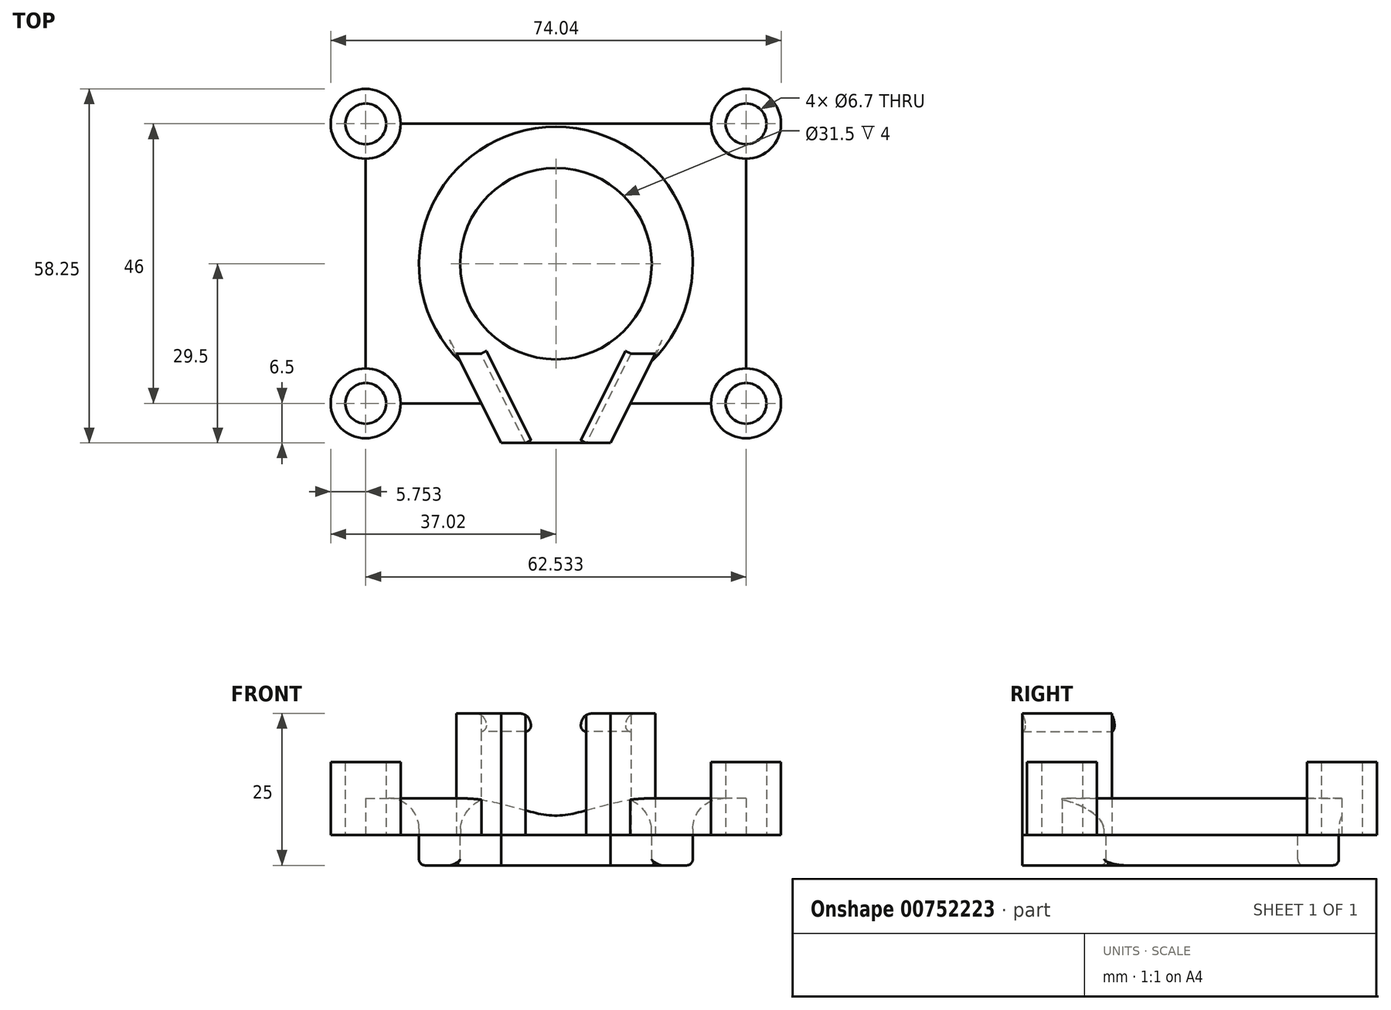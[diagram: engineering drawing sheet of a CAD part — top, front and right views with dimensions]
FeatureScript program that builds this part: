
annotation { "Feature Type Name" : "Feature", "Feature Type Description" : "" }
export const myFeature = defineFeature(function(context is Context, id is Id, definition is map)
    precondition{}
    {
        {
            var Q0;
            Q0=qCreatedBy(makeId("Top.planeOp"),FACE);
            var sketch = newSketch(context, id + "F0", { "sketchPlane" : qUnion([Q0])});
            skCircle(sketch, "E0", {"center": v(-31.27, 23) * mm, "radius": 5.75 * mm});
            skCircle(sketch, "E1", {"center": v(31.27, -23) * mm, "radius": 5.75 * mm});
            skCircle(sketch, "E2", {"center": v(31.27, -23) * mm, "radius": 3.35 * mm});
            skCircle(sketch, "E3", {"center": v(-31.27, 23) * mm, "radius": 3.35 * mm});
            skLineSegment(sketch, "E4", {"start": v(-31.27, 23) * mm, "end": v(31.27, -23) * mm});
            skCircle(sketch, "E5", {"center": v(0, 0) * mm, "radius": 22.5 * mm});
            skCircle(sketch, "E6", {"center": v(0, 0) * mm, "radius": 15.75 * mm});
            skLineSegment(sketch, "E7", {"start": v(-31.27, 23) * mm, "end": v(-31.27, -23) * mm});
            skLineSegment(sketch, "E8", {"start": v(-31.27, -23) * mm, "end": v(31.27, -23) * mm});
            skCircle(sketch, "E9", {"center": v(-31.27, -23) * mm, "radius": 5.75 * mm});
            skCircle(sketch, "E10", {"center": v(-31.27, -23) * mm, "radius": 3.35 * mm});
            skLineSegment(sketch, "E11", {"start": v(-31.27, 23) * mm, "end": v(31.27, 23) * mm});
            skCircle(sketch, "E12", {"center": v(31.27, 23) * mm, "radius": 5.75 * mm});
            skCircle(sketch, "E13", {"center": v(31.27, 23) * mm, "radius": 3.35 * mm});
            skLineSegment(sketch, "E14", {"start": v(31.27, -23) * mm, "end": v(31.27, 23) * mm});
            skLineSegment(sketch, "E15", {"start": v(0, 0) * mm, "end": v(0, -29.5) * mm});
            skLineSegment(sketch, "E16", {"start": v(-5, -29.5) * mm, "end": v(5, -29.5) * mm});
            skLineSegment(sketch, "E17", {"start": v(-5, -29.5) * mm, "end": v(-9, -29.5) * mm});
            skLineSegment(sketch, "E18", {"start": v(5, -29.5) * mm, "end": v(9, -29.5) * mm});
            skLineSegment(sketch, "E19", {"start": v(-5, -29.5) * mm, "end": v(-12.33, -14.82) * mm});
            skLineSegment(sketch, "E20", {"start": v(-12.33, -14.82) * mm, "end": v(12.33, -14.82) * mm});
            skLineSegment(sketch, "E21", {"start": v(12.33, -14.82) * mm, "end": v(5, -29.5) * mm});
            skLineSegment(sketch, "E22", {"start": v(-12.33, -14.82) * mm, "end": v(-16.33, -14.82) * mm});
            skLineSegment(sketch, "E23", {"start": v(-16.33, -14.82) * mm, "end": v(-9, -29.5) * mm});
            skLineSegment(sketch, "E24", {"start": v(9, -29.5) * mm, "end": v(16.32, -14.82) * mm});
            skLineSegment(sketch, "E25", {"start": v(16.32, -14.82) * mm, "end": v(12.33, -14.82) * mm});
            skSolve(sketch);
        }
        {
            var Q0;
            {var subQ0=sQuery(id+"F0.wireOp",EDGE,"E9");var subQ1=sQuery(id+"F0.wireOp",EDGE,"E7");var subQ2=makeQuery(id+"F0.imprint","INTERSECT",VERTEX,{"derivedFrom":[subQ1,subQ0]});Q0=makeQuery(id+"F0.imprint","IMPRINT",FACE,{"disambiguationData":[TD([[makeQuery(id+"F0.imprint","IMPRINT",EDGE,{"disambiguationData":[TD([[subQ2,-1.0]])],"derivedFrom":subQ1}),-1.0]])]});}
            var Q1;
            {var subQ0=sQuery(id+"F0.wireOp",EDGE,"E12");var subQ1=sQuery(id+"F0.wireOp",EDGE,"E11");var subQ2=makeQuery(id+"F0.imprint","INTERSECT",VERTEX,{"derivedFrom":[subQ1,subQ0]});Q1=makeQuery(id+"F0.imprint","IMPRINT",FACE,{"disambiguationData":[TD([[makeQuery(id+"F0.imprint","IMPRINT",EDGE,{"disambiguationData":[TD([[subQ2,-1.0]])],"derivedFrom":subQ1}),1.0]])]});}
            var Q2;
            {var subQ0=sQuery(id+"F0.wireOp",EDGE,"E7");var subQ1=sQuery(id+"F0.wireOp",EDGE,"E0");var subQ2=makeQuery(id+"F0.imprint","INTERSECT",VERTEX,{"derivedFrom":[subQ1,subQ0]});Q2=makeQuery(id+"F0.imprint","IMPRINT",FACE,{"disambiguationData":[TD([[makeQuery(id+"F0.imprint","IMPRINT",EDGE,{"disambiguationData":[TD([[subQ2,1.0]])],"derivedFrom":subQ1}),1.0]])]});}
            var Q3;
            {var subQ0=sQuery(id+"F0.wireOp",EDGE,"E14");var subQ1=sQuery(id+"F0.wireOp",EDGE,"E1");var subQ2=makeQuery(id+"F0.imprint","INTERSECT",VERTEX,{"derivedFrom":[subQ1,subQ0]});Q3=makeQuery(id+"F0.imprint","IMPRINT",FACE,{"disambiguationData":[TD([[makeQuery(id+"F0.imprint","IMPRINT",EDGE,{"disambiguationData":[TD([[subQ2,1.0]])],"derivedFrom":subQ1}),1.0]])]});}
            var Q4;
            {var subQ0=sQuery(id+"F0.wireOp",EDGE,"E9");var subQ1=sQuery(id+"F0.wireOp",EDGE,"E7");var subQ2=makeQuery(id+"F0.imprint","INTERSECT",VERTEX,{"derivedFrom":[subQ1,subQ0]});Q4=makeQuery(id+"F0.imprint","IMPRINT",FACE,{"disambiguationData":[TD([[makeQuery(id+"F0.imprint","IMPRINT",EDGE,{"disambiguationData":[TD([[subQ2,-1.0]])],"derivedFrom":subQ1}),1.0]])]});}
            var Q5;
            {var subQ0=sQuery(id+"F0.wireOp",EDGE,"E12");var subQ1=sQuery(id+"F0.wireOp",EDGE,"E11");var subQ2=makeQuery(id+"F0.imprint","INTERSECT",VERTEX,{"derivedFrom":[subQ1,subQ0]});Q5=makeQuery(id+"F0.imprint","IMPRINT",FACE,{"disambiguationData":[TD([[makeQuery(id+"F0.imprint","IMPRINT",EDGE,{"disambiguationData":[TD([[subQ2,-1.0]])],"derivedFrom":subQ1}),-1.0]])]});}
            var Q6;
            {var subQ0=sQuery(id+"F0.wireOp",EDGE,"E7");var subQ1=sQuery(id+"F0.wireOp",EDGE,"E0");var subQ2=makeQuery(id+"F0.imprint","INTERSECT",VERTEX,{"derivedFrom":[subQ1,subQ0]});Q6=makeQuery(id+"F0.imprint","IMPRINT",FACE,{"disambiguationData":[TD([[makeQuery(id+"F0.imprint","IMPRINT",EDGE,{"disambiguationData":[TD([[subQ2,-1.0]])],"derivedFrom":subQ1}),1.0]])]});}
            var Q7;
            {var subQ0=sQuery(id+"F0.wireOp",EDGE,"E11");var subQ1=sQuery(id+"F0.wireOp",EDGE,"E0");var subQ2=makeQuery(id+"F0.imprint","INTERSECT",VERTEX,{"derivedFrom":[subQ1,subQ0]});Q7=makeQuery(id+"F0.imprint","IMPRINT",FACE,{"disambiguationData":[TD([[makeQuery(id+"F0.imprint","IMPRINT",EDGE,{"disambiguationData":[TD([[subQ2,1.0]])],"derivedFrom":subQ1}),1.0]])]});}
            var Q8;
            {var subQ0=sQuery(id+"F0.wireOp",EDGE,"E14");var subQ1=sQuery(id+"F0.wireOp",EDGE,"E1");var subQ2=makeQuery(id+"F0.imprint","INTERSECT",VERTEX,{"derivedFrom":[subQ1,subQ0]});Q8=makeQuery(id+"F0.imprint","IMPRINT",FACE,{"disambiguationData":[TD([[makeQuery(id+"F0.imprint","IMPRINT",EDGE,{"disambiguationData":[TD([[subQ2,-1.0]])],"derivedFrom":subQ1}),1.0]])]});}
            var Q9;
            {var subQ0=sQuery(id+"F0.wireOp",EDGE,"E8");var subQ1=sQuery(id+"F0.wireOp",EDGE,"E1");var subQ2=makeQuery(id+"F0.imprint","INTERSECT",VERTEX,{"derivedFrom":[subQ1,subQ0]});Q9=makeQuery(id+"F0.imprint","IMPRINT",FACE,{"disambiguationData":[TD([[makeQuery(id+"F0.imprint","IMPRINT",EDGE,{"disambiguationData":[TD([[subQ2,1.0]])],"derivedFrom":subQ1}),1.0]])]});}
            extrude(context, id + "F1", {"entities" : qUnion([Q0, Q1, Q2, Q3, Q4, Q5, Q6, Q7, Q8, Q9]), "depth" : 12 * mm, "offsetDistance" : 25 * mm});
        }
        {
            var Q0;
            {var subQ0=sQuery(id+"F0.wireOp",EDGE,"E5");var subQ1=sQuery(id+"F0.wireOp",EDGE,"E4");var subQ2=makeQuery(id+"F0.imprint","INTERSECT",VERTEX,{"disambiguationData":[OD(0.0)],"derivedFrom":[subQ1,subQ0]});Q0=makeQuery(id+"F0.imprint","IMPRINT",FACE,{"disambiguationData":[TD([[makeQuery(id+"F0.imprint","IMPRINT",EDGE,{"disambiguationData":[TD([[subQ2,-1.0]])],"derivedFrom":subQ1}),1.0]])]});}
            var Q1;
            {var subQ0=sQuery(id+"F0.wireOp",EDGE,"E5");var subQ1=sQuery(id+"F0.wireOp",EDGE,"E4");var subQ2=makeQuery(id+"F0.imprint","INTERSECT",VERTEX,{"disambiguationData":[OD(0.0)],"derivedFrom":[subQ1,subQ0]});Q1=makeQuery(id+"F0.imprint","IMPRINT",FACE,{"disambiguationData":[TD([[makeQuery(id+"F0.imprint","IMPRINT",EDGE,{"disambiguationData":[TD([[subQ2,-1.0]])],"derivedFrom":subQ1}),-1.0]])]});}
            var Q2;
            {var subQ0=sQuery(id+"F0.wireOp",EDGE,"E25");Q2=makeQuery(id+"F0.imprint","IMPRINT",FACE,{"disambiguationData":[TD([[makeQuery(id+"F0.imprint","IMPRINT",EDGE,{"derivedFrom":subQ0}),-1.0]])]});}
            var Q3;
            {var subQ5=sQuery(id+"F0.wireOp",EDGE,"E25");Q3=makeQuery(id+"F0.imprint","IMPRINT",FACE,{"disambiguationData":[TD([[makeQuery(id+"F0.imprint","IMPRINT",EDGE,{"derivedFrom":subQ5}),1.0]])]});}
            var Q4;
            {var subQ5=sQuery(id+"F0.wireOp",EDGE,"E15");var subQ6=sQuery(id+"F0.wireOp",EDGE,"E5");var subQ7=makeQuery(id+"F0.imprint","INTERSECT",VERTEX,{"derivedFrom":[subQ6,subQ5]});Q4=makeQuery(id+"F0.imprint","IMPRINT",FACE,{"disambiguationData":[TD([[makeQuery(id+"F0.imprint","IMPRINT",EDGE,{"disambiguationData":[TD([[subQ7,-1.0]])],"derivedFrom":subQ6}),1.0]])]});}
            var Q5;
            {var subQ1=sQuery(id+"F0.wireOp",EDGE,"E19");var subQ3=sQuery(id+"F0.wireOp",EDGE,"E5");var subQ4=makeQuery(id+"F0.imprint","INTERSECT",VERTEX,{"derivedFrom":[subQ3,subQ1]});Q5=makeQuery(id+"F0.imprint","IMPRINT",FACE,{"disambiguationData":[TD([[makeQuery(id+"F0.imprint","IMPRINT",EDGE,{"disambiguationData":[TD([[subQ4,-1.0]])],"derivedFrom":subQ3}),1.0]])]});}
            var Q6;
            {var subQ5=sQuery(id+"F0.wireOp",EDGE,"E22");Q6=makeQuery(id+"F0.imprint","IMPRINT",FACE,{"disambiguationData":[TD([[makeQuery(id+"F0.imprint","IMPRINT",EDGE,{"derivedFrom":subQ5}),1.0]])]});}
            var Q7;
            {var subQ0=sQuery(id+"F0.wireOp",EDGE,"E23");var subQ1=sQuery(id+"F0.wireOp",EDGE,"E5");var subQ2=makeQuery(id+"F0.imprint","INTERSECT",VERTEX,{"derivedFrom":[subQ1,subQ0]});Q7=makeQuery(id+"F0.imprint","IMPRINT",FACE,{"disambiguationData":[TD([[makeQuery(id+"F0.imprint","IMPRINT",EDGE,{"disambiguationData":[TD([[subQ2,-1.0]])],"derivedFrom":subQ1}),-1.0]])]});}
            var Q8;
            {var subQ5=sQuery(id+"F0.wireOp",EDGE,"E17");Q8=makeQuery(id+"F0.imprint","IMPRINT",FACE,{"disambiguationData":[TD([[makeQuery(id+"F0.imprint","IMPRINT",EDGE,{"derivedFrom":subQ5}),-1.0]])]});}
            var Q9;
            {var subQ0=sQuery(id+"F0.wireOp",EDGE,"E19");var subQ1=sQuery(id+"F0.wireOp",EDGE,"E8");var subQ2=makeQuery(id+"F0.imprint","INTERSECT",VERTEX,{"derivedFrom":[subQ1,subQ0]});Q9=makeQuery(id+"F0.imprint","IMPRINT",FACE,{"disambiguationData":[TD([[makeQuery(id+"F0.imprint","IMPRINT",EDGE,{"disambiguationData":[TD([[subQ2,-1.0]])],"derivedFrom":subQ1}),-1.0]])]});}
            var Q10;
            {var subQ0=sQuery(id+"F0.wireOp",EDGE,"E19");var subQ1=sQuery(id+"F0.wireOp",EDGE,"E5");var subQ2=makeQuery(id+"F0.imprint","INTERSECT",VERTEX,{"derivedFrom":[subQ1,subQ0]});Q10=makeQuery(id+"F0.imprint","IMPRINT",FACE,{"disambiguationData":[TD([[makeQuery(id+"F0.imprint","IMPRINT",EDGE,{"disambiguationData":[TD([[subQ2,-1.0]])],"derivedFrom":subQ1}),-1.0]])]});}
            var Q11;
            {var subQ0=sQuery(id+"F0.wireOp",EDGE,"E15");var subQ1=sQuery(id+"F0.wireOp",EDGE,"E8");var subQ2=makeQuery(id+"F0.imprint","INTERSECT",VERTEX,{"derivedFrom":[subQ1,subQ0]});Q11=makeQuery(id+"F0.imprint","IMPRINT",FACE,{"disambiguationData":[TD([[makeQuery(id+"F0.imprint","IMPRINT",EDGE,{"disambiguationData":[TD([[subQ2,-1.0]])],"derivedFrom":subQ1}),-1.0]])]});}
            var Q12;
            {var subQ0=sQuery(id+"F0.wireOp",EDGE,"E15");var subQ1=sQuery(id+"F0.wireOp",EDGE,"E5");var subQ2=makeQuery(id+"F0.imprint","INTERSECT",VERTEX,{"derivedFrom":[subQ1,subQ0]});Q12=makeQuery(id+"F0.imprint","IMPRINT",FACE,{"disambiguationData":[TD([[makeQuery(id+"F0.imprint","IMPRINT",EDGE,{"disambiguationData":[TD([[subQ2,-1.0]])],"derivedFrom":subQ1}),-1.0]])]});}
            var Q13;
            {var subQ5=sQuery(id+"F0.wireOp",EDGE,"E18");Q13=makeQuery(id+"F0.imprint","IMPRINT",FACE,{"disambiguationData":[TD([[makeQuery(id+"F0.imprint","IMPRINT",EDGE,{"derivedFrom":subQ5}),1.0]])]});}
            var Q14;
            {var subQ0=sQuery(id+"F0.wireOp",EDGE,"E21");var subQ1=sQuery(id+"F0.wireOp",EDGE,"E5");var subQ2=makeQuery(id+"F0.imprint","INTERSECT",VERTEX,{"derivedFrom":[subQ1,subQ0]});Q14=makeQuery(id+"F0.imprint","IMPRINT",FACE,{"disambiguationData":[TD([[makeQuery(id+"F0.imprint","IMPRINT",EDGE,{"disambiguationData":[TD([[subQ2,-1.0]])],"derivedFrom":subQ1}),-1.0]])]});}
            extrude(context, id + "F2", {"entities" : qUnion([Q0, Q1, Q2, Q3, Q4, Q5, Q6, Q7, Q8, Q9, Q10, Q11, Q12, Q13, Q14]), "depth" : -5 * mm, "offsetDistance" : 25 * mm});
        }
        {
            var Q0;
            {var subQ5=sQuery(id+"F0.wireOp",EDGE,"E0");var subQ11=sQuery(id+"F0.wireOp",EDGE,"E11");var subQ14=makeQuery(id+"F0.imprint","INTERSECT",VERTEX,{"derivedFrom":[subQ5,subQ11]});Q0=makeQuery(id+"F0.imprint","IMPRINT",FACE,{"disambiguationData":[TD([[makeQuery(id+"F0.imprint","IMPRINT",EDGE,{"disambiguationData":[TD([[subQ14,1.0]])],"derivedFrom":subQ5}),-1.0]])]});}
            var Q1;
            {var subQ7=sQuery(id+"F0.wireOp",EDGE,"E0");var subQ9=sQuery(id+"F0.wireOp",EDGE,"E7");var subQ10=makeQuery(id+"F0.imprint","INTERSECT",VERTEX,{"derivedFrom":[subQ7,subQ9]});Q1=makeQuery(id+"F0.imprint","IMPRINT",FACE,{"disambiguationData":[TD([[makeQuery(id+"F0.imprint","IMPRINT",EDGE,{"disambiguationData":[TD([[subQ10,-1.0]])],"derivedFrom":subQ7}),-1.0]])]});}
            var Q2;
            {var subQ0=sQuery(id+"F0.wireOp",EDGE,"E8");var subQ1=sQuery(id+"F0.wireOp",EDGE,"E1");var subQ2=makeQuery(id+"F0.imprint","INTERSECT",VERTEX,{"derivedFrom":[subQ1,subQ0]});Q2=makeQuery(id+"F0.imprint","IMPRINT",FACE,{"disambiguationData":[TD([[makeQuery(id+"F0.imprint","IMPRINT",EDGE,{"disambiguationData":[TD([[subQ2,1.0]])],"derivedFrom":subQ1}),-1.0]])]});}
            extrude(context, id + "F3", {"entities" : qUnion([Q0, Q1, Q2]), "depth" : 6 * mm, "offsetDistance" : 25 * mm});
        }
        {
            var Q0;
            Q0=makeQuery(id+"F3.opExtrude","CAP_EDGE",EDGE,{"disambiguationData":[OSD([sQuery(id+"F0.wireOp",EDGE,"E5")])],"isStart":false});
            fillet(context, id + "F4", {"entities" : qUnion([Q0]), "radius" : 5 * mm, "tangentPropagation" : true, "allowEdgeOverflow" : false});
        }
        {
            var Q0;
            {var subQ5=sQuery(id+"F0.wireOp",EDGE,"E22");Q0=makeQuery(id+"F0.imprint","IMPRINT",FACE,{"disambiguationData":[TD([[makeQuery(id+"F0.imprint","IMPRINT",EDGE,{"derivedFrom":subQ5}),1.0]])]});}
            var Q1;
            {var subQ0=sQuery(id+"F0.wireOp",EDGE,"E23");var subQ1=sQuery(id+"F0.wireOp",EDGE,"E5");var subQ2=makeQuery(id+"F0.imprint","INTERSECT",VERTEX,{"derivedFrom":[subQ1,subQ0]});Q1=makeQuery(id+"F0.imprint","IMPRINT",FACE,{"disambiguationData":[TD([[makeQuery(id+"F0.imprint","IMPRINT",EDGE,{"disambiguationData":[TD([[subQ2,-1.0]])],"derivedFrom":subQ1}),-1.0]])]});}
            var Q2;
            {var subQ5=sQuery(id+"F0.wireOp",EDGE,"E17");Q2=makeQuery(id+"F0.imprint","IMPRINT",FACE,{"disambiguationData":[TD([[makeQuery(id+"F0.imprint","IMPRINT",EDGE,{"derivedFrom":subQ5}),-1.0]])]});}
            var Q3;
            {var subQ5=sQuery(id+"F0.wireOp",EDGE,"E18");Q3=makeQuery(id+"F0.imprint","IMPRINT",FACE,{"disambiguationData":[TD([[makeQuery(id+"F0.imprint","IMPRINT",EDGE,{"derivedFrom":subQ5}),1.0]])]});}
            var Q4;
            {var subQ0=sQuery(id+"F0.wireOp",EDGE,"E21");var subQ1=sQuery(id+"F0.wireOp",EDGE,"E5");var subQ2=makeQuery(id+"F0.imprint","INTERSECT",VERTEX,{"derivedFrom":[subQ1,subQ0]});Q4=makeQuery(id+"F0.imprint","IMPRINT",FACE,{"disambiguationData":[TD([[makeQuery(id+"F0.imprint","IMPRINT",EDGE,{"disambiguationData":[TD([[subQ2,-1.0]])],"derivedFrom":subQ1}),-1.0]])]});}
            var Q5;
            {var subQ5=sQuery(id+"F0.wireOp",EDGE,"E25");Q5=makeQuery(id+"F0.imprint","IMPRINT",FACE,{"disambiguationData":[TD([[makeQuery(id+"F0.imprint","IMPRINT",EDGE,{"derivedFrom":subQ5}),1.0]])]});}
            extrude(context, id + "F5", {"entities" : qUnion([Q0, Q1, Q2, Q3, Q4, Q5]), "depth" : 20 * mm, "offsetDistance" : 25 * mm});
        }
        {
            var Q0;
            Q0=makeQuery(id+"F5.opExtrude","SWEPT_FACE",FACE,{"disambiguationData":[OSD([sQuery(id+"F0.wireOp",EDGE,"E19")])]});
            var sketch = newSketch(context, id + "F6", { "sketchPlane" : qUnion([Q0])});
            skLineSegment(sketch, "E26.bottom", {"start": v(-24.16, 20) * mm, "end": v(-7.76, 20) * mm});
            skLineSegment(sketch, "E26.top", {"start": v(-24.16, 17) * mm, "end": v(-7.76, 17) * mm});
            skLineSegment(sketch, "E26.left", {"start": v(-24.16, 20) * mm, "end": v(-24.16, 17) * mm});
            skLineSegment(sketch, "E26.right", {"start": v(-7.76, 20) * mm, "end": v(-7.76, 17) * mm});
            skSolve(sketch);
        }
        {
            var Q0;
            Q0 = qSketchRegion(id + "F6", true);
            extrude(context, id + "F7", {"entities" : qUnion([Q0]), "operationType" : NewBodyOperationType.ADD, "depth" : 1 * mm, "offsetDistance" : 25 * mm});
        }
        {
            var Q0;
            Q0=makeQuery(id+"F7.opExtrude","CAP_EDGE",EDGE,{"disambiguationData":[OSD([sQuery(id+"F6.wireOp",EDGE,"E26.bottom")])],"isStart":false});
            fillet(context, id + "F8", {"entities" : qUnion([Q0]), "radius" : 2 * mm, "tangentPropagation" : true, "allowEdgeOverflow" : false});
        }
        {
            var Q0;
            Q0=makeQuery(id+"F7.opExtrude","CAP_EDGE",EDGE,{"disambiguationData":[OSD([sQuery(id+"F6.wireOp",EDGE,"E26.top")])],"isStart":false});
            fillet(context, id + "F9", {"entities" : qUnion([Q0]), "radius" : 1 * mm, "tangentPropagation" : true, "allowEdgeOverflow" : false});
        }
        {
            var Q0;
            Q0=makeQuery(id+"F5.opExtrude","SWEPT_FACE",FACE,{"disambiguationData":[OSD([sQuery(id+"F0.wireOp",EDGE,"E21")])]});
            var sketch = newSketch(context, id + "F10", { "sketchPlane" : qUnion([Q0])});
            skLineSegment(sketch, "E27.bottom", {"start": v(7.76, 20) * mm, "end": v(24.16, 20) * mm});
            skLineSegment(sketch, "E27.top", {"start": v(7.76, 17) * mm, "end": v(24.16, 17) * mm});
            skLineSegment(sketch, "E27.left", {"start": v(7.76, 20) * mm, "end": v(7.76, 17) * mm});
            skLineSegment(sketch, "E27.right", {"start": v(24.16, 20) * mm, "end": v(24.16, 17) * mm});
            skSolve(sketch);
        }
        {
            var Q0;
            Q0=makeQuery(id+"F10.imprint","IMPRINT",FACE,{"disambiguationData":[TD([[makeQuery(id+"F10.imprint","IMPRINT",EDGE,{"derivedFrom":sQuery(id+"F10.wireOp",EDGE,"E27.bottom")}),-1.0]])]});
            extrude(context, id + "F11", {"entities" : qUnion([Q0]), "operationType" : NewBodyOperationType.ADD, "depth" : 1 * mm, "offsetDistance" : 25 * mm});
        }
        {
            var Q0;
            Q0=makeQuery(id+"F11.opExtrude","CAP_EDGE",EDGE,{"disambiguationData":[OSD([sQuery(id+"F10.wireOp",EDGE,"E27.bottom")])],"isStart":false});
            fillet(context, id + "F12", {"entities" : qUnion([Q0]), "radius" : 2 * mm, "tangentPropagation" : true, "allowEdgeOverflow" : false});
        }
        {
            var Q0;
            Q0=makeQuery(id+"F11.opExtrude","CAP_EDGE",EDGE,{"disambiguationData":[OSD([sQuery(id+"F10.wireOp",EDGE,"E27.top")])],"isStart":false});
            fillet(context, id + "F13", {"entities" : qUnion([Q0]), "radius" : 1 * mm, "tangentPropagation" : true, "allowEdgeOverflow" : false});
        }
        {
            var Q0;
            Q0=makeQuery(id+"F2.opExtrude","CAP_EDGE",EDGE,{"disambiguationData":[OSD([sQuery(id+"F0.wireOp",EDGE,"E5")])],"isStart":false});
            fillet(context, id + "F14", {"entities" : qUnion([Q0]), "radius" : 1 * mm, "tangentPropagation" : true, "allowEdgeOverflow" : false});
        }
        {
            var Q0;
            Q0=makeQuery(id+"F14.opFillet","BLEND_FACE",FACE,{"disambiguationData":[OSD([sQuery(id+"F0.wireOp",EDGE,"E5")])]});
            fillet(context, id + "F15", {"entities" : qUnion([Q0]), "radius" : 1 * mm, "tangentPropagation" : true, "allowEdgeOverflow" : false});
        }
        {
            var Q0;
            Q0=makeQuery(id+"F2.opExtrude","CAP_EDGE",EDGE,{"disambiguationData":[OSD([sQuery(id+"F0.wireOp",EDGE,"E6")])],"isStart":false});
            fillet(context, id + "F16", {"entities" : qUnion([Q0]), "radius" : 1 * mm, "tangentPropagation" : true, "allowEdgeOverflow" : false});
        }
    });
